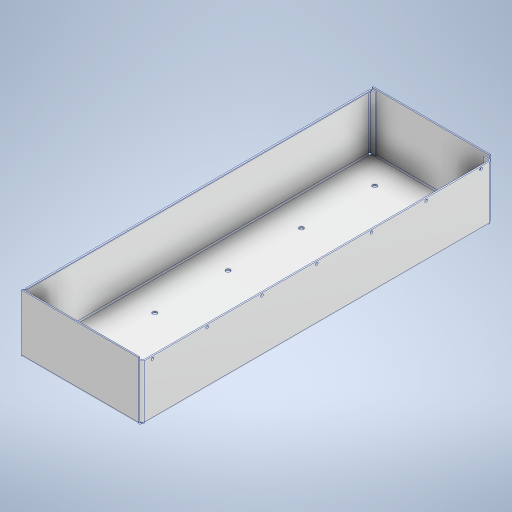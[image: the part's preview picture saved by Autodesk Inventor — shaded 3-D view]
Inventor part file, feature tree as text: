
AUTODESK INVENTOR PART (.ipt)
format: ipt  version: 2023 (Build 270158000, 158)  size: 481,792 bytes
history: native  units: in
note: dims shown in document units (in); Inventor stores cm internally (conversion verified against a paired STEP export)
features: sheet_metal_op x16, sketch x12, other x10, hole x2, pattern_linear x2
ambient origin geometry x8: Origin, YZ Plane, XZ Plane, XY Plane, X Axis, Y Axis, Z Axis, Center Point
bodies: Solid1 (feature_tree)
feature tree (42):
  sheet_metal_op  "Face1"
  hole  "Hole1"  [1 undecoded]
  pattern_linear  "Rectangular Pattern1"  Count1=30  [1 undecoded]
  sheet_metal_op  "Flange4"
  sheet_metal_op  "Flange5"
  sheet_metal_op  "Flange11"
  sketch  "Sketch21"  dims[d51=0.0438in]
  hole  "Hole2"  [1 undecoded]
  pattern_linear  "Rectangular Pattern2"  Count1=5  [1 undecoded]
  sheet_metal_op  "Flange14"
  sheet_metal_op  "Flange15"
  sketch  "Sketch1"  dims[d0=23.622in d1=7.874in d2=11.811in]
  other  "Plate1"
  sketch  "Sketch2"  dims[d3=3.937in d4=0.0875in]
  sketch  "Sketch6"  dims[d5=0.2969in d6=0.2953in d7=0.1476in d8=0.0984in d9=90.0deg d10=0.0875in]
  other  "Plate5"
  sheet_metal_op  "Bend4"
  sheet_metal_op  "Corner4"
  sketch  "Sketch7"  dims[d11=0.0in d12=1.9685in]
  other  "Plate6"
  sheet_metal_op  "Bend5"
  sheet_metal_op  "Corner5"
  sketch  "Sketch8"  dims[d13=2.0669in]
  sketch  "Sketch9"  dims[d14=0.7874in d16=3.937in]
  sketch  "Sketch17"  dims[d17=1.9685in d19=4.9213in]
  other  "Plate12"
  sheet_metal_op  "Bend11"
  sheet_metal_op  "Corner11"
  sketch  "Sketch20"  dims[d50=0.0875in]
  sketch  "Sketch22"  dims[d52=0.175in]
  sketch  "Sketch23"  dims[d53=0.0875in]
  other  "Plate15"
  sheet_metal_op  "Bend14"
  sheet_metal_op  "Corner14"
  sketch  "Sketch24"  dims[d54=3.937in d55=90.0deg d56=0.0787in d57=0.35in d58=0.0875in d59=0.0875in d60=0.0875in d61=0.0438in d62=0.175in d63=0.0875in d64=3.937in d65=90.0deg d66=0.0787in d67=0.35in d68=0.0875in d69=0.0875in d70=0.0098in d71=0.0591in d72=0.0098in d73=0.0591in d78=0.0875in d79=0.0in d80=0.0875in d81=0.0in d147=0.0875in d148=0.0438in d149=0.175in d150=0.0875in d151=0.4921in d152=90.0deg d153=0.0787in d154=0.35in d155=0.0875in d156=0.0875in d177=0.194in d178=0.2953in d179=0.1476in d180=0.0984in d181=90.0deg d182=0.0875in d183=0.8108in d185=0.5in d186=2.7559in d188=3.6755in d190=0.0875in d191=0.0in d192=0.162in d193=0.2073in d195=0.0875in d196=0.0in d197=0.1094in d198=0.0875in d199=0.0438in d200=0.175in d201=0.0875in d202=0.2953in d203=90.0deg d204=0.0591in d205=0.35in d206=0.0875in d207=0.0875in d208=0.0875in d209=0.0438in d210=0.175in d211=0.0875in d212=0.1969in d213=90.0deg d214=0.0591in d215=0.35in d216=0.0875in d217=0.0875in]
  other  "Plate16"
  sheet_metal_op  "Bend15"
  sheet_metal_op  "Corner15"
  other  "Cut2"
  other  "Cut3"
  other  "Cut4"
  other  "Cut5"
note: 4 required parameter values undecoded (feature->parameter linkage not recoverable at this tier; creation-order binding heuristic only, values carry confidence <= 0.55)
